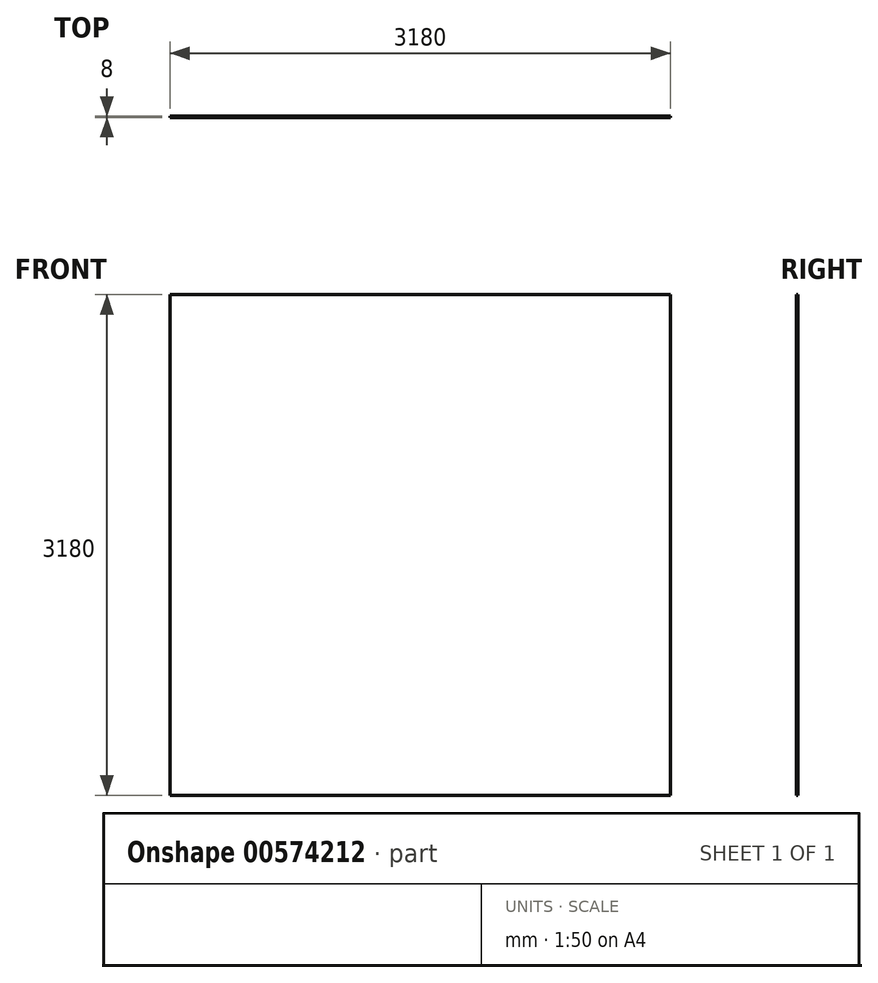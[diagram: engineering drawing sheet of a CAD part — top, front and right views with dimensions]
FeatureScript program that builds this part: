
annotation { "Feature Type Name" : "Feature", "Feature Type Description" : "" }
export const myFeature = defineFeature(function(context is Context, id is Id, definition is map)
    precondition{}
    {
        {
            var Q0;
            Q0=qCreatedBy(makeId("Front.planeOp"),FACE);
            var sketch = newSketch(context, id + "F0", { "sketchPlane" : qUnion([Q0])});
            skLineSegment(sketch, "E0.bottom", {"start": v(0, 0) * mm, "end": v(3180, 0) * mm});
            skLineSegment(sketch, "E0.top", {"start": v(0, 3180) * mm, "end": v(3180, 3180) * mm});
            skLineSegment(sketch, "E0.left", {"start": v(0, 0) * mm, "end": v(0, 3180) * mm});
            skLineSegment(sketch, "E0.right", {"start": v(3180, 0) * mm, "end": v(3180, 3180) * mm});
            skSolve(sketch);
        }
        {
            var Q0;
            Q0=makeQuery(id+"F0.imprint","IMPRINT",FACE,{"disambiguationData":[TD([[makeQuery(id+"F0.imprint","IMPRINT",EDGE,{"derivedFrom":sQuery(id+"F0.wireOp",EDGE,"E0.bottom")}),1.0]])]});
            extrude(context, id + "F1", {"entities" : qUnion([Q0]), "depth" : 8 * mm, "offsetDistance" : 25 * mm});
        }
    });
